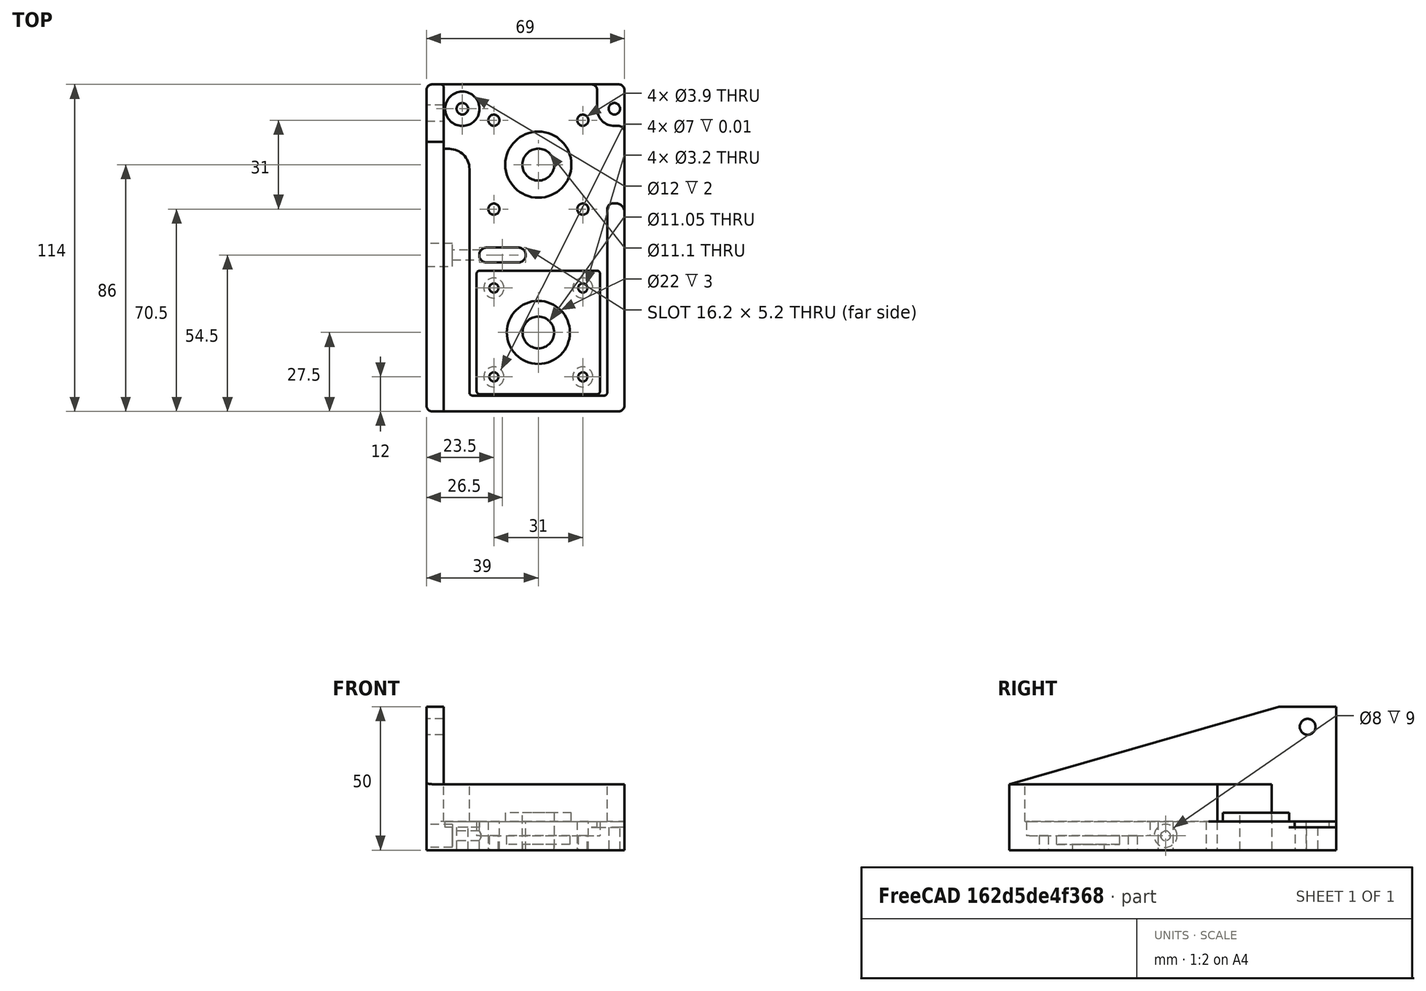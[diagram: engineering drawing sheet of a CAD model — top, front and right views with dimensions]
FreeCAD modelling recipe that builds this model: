
FCSTD DOCUMENT  (FreeCAD 0.19R)
Label: BeltDriveUnit3
License: All rights reserved
LicenseURL: http://en.wikipedia.org/wiki/All_rights_reserved
objects: Sketcher::SketchObject×14, PartDesign::Pocket×10, PartDesign::Fillet×10, PartDesign::Pad×4, PartDesign::Body×1, Mesh::Feature×1
note: 63 computed .brp shape members not serialized (recipe doc carries the construction recipe); baked Part::Feature solids carry a one-line shape summary decoded from their .brp

FEATURE [Sketcher::SketchObject] Sketch
  FullyConstrained = false
  MapMode = 5
  Support = -> [XY_Plane]
  sketch-geometry (17):
    g0: LineSegment StartX=-33 StartY=28 StartZ=0 EndX=30 EndY=28 EndZ=0
    g1: LineSegment StartX=30 StartY=28 StartZ=0 EndX=30 EndY=-86 EndZ=0
    g2: LineSegment StartX=30 StartY=-86 StartZ=0 EndX=-33 EndY=-86 EndZ=0
    g3: LineSegment StartX=-33 StartY=-86 StartZ=0 EndX=-33 EndY=28 EndZ=0
    g4: LineSegment StartX=-21 StartY=21 StartZ=0 EndX=21 EndY=21 EndZ=0
    g5: LineSegment StartX=21 StartY=21 StartZ=0 EndX=21 EndY=-21 EndZ=0
    g6: LineSegment StartX=21 StartY=-21 StartZ=0 EndX=-21 EndY=-21 EndZ=0
    g7: LineSegment StartX=-21 StartY=-21 StartZ=0 EndX=-21 EndY=21 EndZ=0
    g8: Circle CenterX=-15.5 CenterY=15.5 CenterZ=0 NormalX=0 NormalY=0 NormalZ=1 AngleXU=0 Radius=1.95
    g9: Circle CenterX=15.5 CenterY=15.5 CenterZ=0 NormalX=0 NormalY=0 NormalZ=1 AngleXU=0 Radius=1.95
    g10: Circle CenterX=-15.5 CenterY=-15.5 CenterZ=0 NormalX=0 NormalY=0 NormalZ=1 AngleXU=0 Radius=1.95
    g11: Circle CenterX=15.5 CenterY=-15.5 CenterZ=0 NormalX=0 NormalY=0 NormalZ=1 AngleXU=0 Radius=1.95
    g12: Circle CenterX=0 CenterY=-58.5 CenterZ=0 NormalX=0 NormalY=0 NormalZ=1 AngleXU=0 Radius=5.525
    g13: Circle CenterX=-15.5 CenterY=-43 CenterZ=0 NormalX=0 NormalY=0 NormalZ=1 AngleXU=0 Radius=1.6
    g14: Circle CenterX=15.5 CenterY=-43 CenterZ=0 NormalX=0 NormalY=0 NormalZ=1 AngleXU=0 Radius=1.6
    g15: Circle CenterX=-15.5 CenterY=-74 CenterZ=0 NormalX=0 NormalY=0 NormalZ=1 AngleXU=0 Radius=1.6
    g16: Circle CenterX=15.5 CenterY=-74 CenterZ=0 NormalX=0 NormalY=0 NormalZ=1 AngleXU=0 Radius=1.6
  constraints (44):
    c: Coincident(g0,g1)
    c: Coincident(g1,g2)
    c: Coincident(g2,g3)
    c: Coincident(g3,g0)
    c: Horizontal(g2)
    c: Vertical(g1)
    c: Vertical(g3)
    c: Coincident(g4,g5)
    c: Coincident(g5,g6)
    c: Coincident(g6,g7)
    c: Coincident(g7,g4)
    c: Horizontal(g4)
    c: Horizontal(g6)
    c: Vertical(g5)
    c: Vertical(g7)
    c: Equal(g5,g4)
    c: Distance(g5) = 42
    c: Symmetric(g4,g6,g-1)
    c: Distance(g4,g0) = 7
    c: Diameter(g11) = 3.9
    c: Equal(g11,g10)
    c: Equal(g11,g8)
    c: Equal(g11,g9)
    c: Distance(g9,g8) = 31
    c: Symmetric(g9,g8,g-2)
    c: Distance(g10,g8) = 31
    c: DistanceY(g11,g9) = 31
    c: DistanceX(g10,g11) = 31
    c: Symmetric(g9,g10,g-1)
    c: Diameter(g16) = 3.2
    c: Equal(g16,g14)
    c: Equal(g16,g13)
    c: Equal(g16,g15)
    c: Symmetric(g14,g13,g-2)
    c: Symmetric(g16,g15,g-2)
    c: Symmetric(g16,g13,g12)
    c: PointOnObject(g12,g-2)
    c: Distance(g14,g13) = 31
    c: Distance(g16,g14) = 31
    c: Distance(g-1,g12) = 58.5
    c: Diameter(g12) = 11.05
    c: DistanceY(g1) = -86
    c: DistanceX(g0) = 30
    c: DistanceX(g0) = -33
FEATURE [PartDesign::Pad] Pad
  Direction = (1,1,1)
  Length = 10
  Length2 = 100
  Profile = -> Sketch
  Type = 0
FEATURE [Sketcher::SketchObject] Sketch004  label="StepperPlugArtillery"
  FullyConstrained = true
  MapMode = 5
  Placement = pos=(0,0,10) rot=(0,0,1;0rad)
  Support = -> [Pad]
  sketch-geometry (1):
    g0: Circle CenterX=0 CenterY=0 CenterZ=0 NormalX=0 NormalY=0 NormalZ=1 AngleXU=0 Radius=11.525
  constraints (2):
    c: Coincident(g0,g-1)
    c: Diameter(g0) = 23.05
FEATURE [PartDesign::Pad] Pad001
  BaseFeature = -> Pad
  Direction = (1,1,1)
  Length = 3
  Length2 = 100
  Profile = -> Sketch004
  Type = 0
FEATURE [Sketcher::SketchObject] Sketch003  label="BearingBore"
  FullyConstrained = false
  MapMode = 5
  Placement = pos=(0,0,13) rot=(0,0,1;0rad)
  Support = -> [Pad001]
  sketch-geometry (1):
    g0: Circle CenterX=0 CenterY=0 CenterZ=0 NormalX=0 NormalY=0 NormalZ=1 AngleXU=0 Radius=5.55
  constraints (1):
    c: Diameter(g0) = 11.1
FEATURE [PartDesign::Pocket] Pocket
  BaseFeature = -> Pad001
  Length = 5
  Length2 = 100
  Profile = -> Sketch003
  Type = 1
FEATURE [Sketcher::SketchObject] Sketch006  label="StepperSocket"
  ExternalGeometry = -> [Pocket]
  FullyConstrained = true
  MapMode = 5
  Placement = pos=(0,0,10) rot=(0,0,1;0rad)
  Support = -> [Pocket]
  sketch-geometry (1):
    g0: Circle CenterX=0 CenterY=-58.5 CenterZ=0 NormalX=0 NormalY=0 NormalZ=1 AngleXU=0 Radius=11
  constraints (2):
    c: Coincident(g0,g-3)
    c: Diameter(g0) = 22
FEATURE [PartDesign::Pocket] Pocket001
  BaseFeature = -> Pocket
  Length = 8
  Length2 = 100
  Profile = -> Sketch006
  Type = 0
FEATURE [Sketcher::SketchObject] Sketch007
  ExternalGeometry = -> [Pocket001]
  FullyConstrained = true
  MapMode = 5
  Placement = pos=(0,0,0) rot=(1,0,0;3.14159rad)
  Support = -> [Pocket001]
  sketch-geometry (4):
    g0: Circle CenterX=-15.5 CenterY=74 CenterZ=0 NormalX=0 NormalY=0 NormalZ=1 AngleXU=0 Radius=3.5
    g1: Circle CenterX=15.5 CenterY=74 CenterZ=0 NormalX=0 NormalY=0 NormalZ=1 AngleXU=0 Radius=3.5
    g2: Circle CenterX=15.5 CenterY=43 CenterZ=0 NormalX=0 NormalY=0 NormalZ=1 AngleXU=0 Radius=3.5
    g3: Circle CenterX=-15.5 CenterY=43 CenterZ=0 NormalX=0 NormalY=0 NormalZ=1 AngleXU=0 Radius=3.5
  constraints (9):
    c: Diameter(g3) = 7
    c: Equal(g3,g1)
    c: Equal(g3,g2)
    c: Equal(g3,g0)
    c: Symmetric(g0,g2,g-3)
    c: Symmetric(g1,g3,g-3)
    c: Distance(g2,g1) = 31
    c: Distance(g3,g2) = 31
    c: Symmetric(g3,g2,g-2)
FEATURE [PartDesign::Pocket] Pocket002
  BaseFeature = -> Pocket001
  Length = 0.01
  Length2 = 100
  Profile = -> Sketch007
  Type = 0
FEATURE [Sketcher::SketchObject] Sketch008  label="Slot"
  ExternalGeometry = -> [Pocket002]
  FullyConstrained = true
  MapMode = 5
  Placement = pos=(0,0,10) rot=(0,0,1;0rad)
  Support = -> [Pocket002]
  sketch-geometry (11):
    g0: Circle CenterX=0 CenterY=0 CenterZ=0 NormalX=0 NormalY=0 NormalZ=1 AngleXU=0 Radius=18.5
    g1: Circle CenterX=0 CenterY=-58.5 CenterZ=0 NormalX=0 NormalY=0 NormalZ=1 AngleXU=0 Radius=6
    g2: LineSegment StartX=-18.0727 StartY=-3.95299 StartZ=0 EndX=-5.86143 EndY=-59.782 EndZ=0
    g3: ArcOfCircle CenterX=-18 CenterY=-31.5 CenterZ=0 NormalX=0 NormalY=0 NormalZ=1 AngleXU=0 Radius=2.6 StartAngle=1.5708 EndAngle=4.71239
    g4: ArcOfCircle CenterX=-7 CenterY=-31.5 CenterZ=0 NormalX=0 NormalY=0 NormalZ=1 AngleXU=0 Radius=2.6 StartAngle=4.71239 EndAngle=7.85398
    g5: LineSegment StartX=-18 StartY=-34.1 StartZ=0 EndX=-7 EndY=-34.1 EndZ=0
    g6: LineSegment StartX=-18 StartY=-28.9 StartZ=0 EndX=-7 EndY=-28.9 EndZ=0
    g7: Circle CenterX=-18 CenterY=-31.5 CenterZ=0 NormalX=0 NormalY=0 NormalZ=1 AngleXU=0 Radius=6
    g8: Circle CenterX=-7 CenterY=-31.5 CenterZ=0 NormalX=0 NormalY=0 NormalZ=1 AngleXU=0 Radius=6
    g9: LineSegment StartX=-15.5 StartY=-37.5 StartZ=0 EndX=-15.5 EndY=-79 EndZ=0
    g10: LineSegment StartX=-15.5 StartY=-31.5 StartZ=0 EndX=-15.5 EndY=-37.5 EndZ=0
  constraints (29):
    c: Diameter(g0) = 37
    c: Coincident(g0,g-1)
    c: Diameter(g1) = 12
    c: Coincident(g1,g-3)
    c: PointOnObject(g2,g0)
    c: PointOnObject(g2,g1)
    c: Tangent(g2,g0)
    c: Tangent(g1,g2)
    c: Tangent(g3,g6) = 1.5708
    c: Tangent(g3,g5) = -1.5708
    c: Tangent(g5,g4) = -1.5708
    c: Tangent(g6,g4) = 1.5708
    c: Horizontal(g5)
    c: Equal(g3,g4)
    c: Diameter(g7) = 12
    c: Coincident(g3,g7)
    c: Diameter(g8) = 12
    c: Coincident(g8,g4)
    c: Distance(g3,g3) = 5.2
    c: Distance(g6) = 11
    c: DistanceX(g4) = -7
    c: Vertical(g9)
    c: Distance(g9) = 41.5
    c: PointOnObject(g-5,g9)
    c: DistanceY(g-5,g9) = 5.5
    c: Vertical(g10)
    c: Distance(g10) = 6
    c: Coincident(g10,g9)
    c: DistanceY(g10,g3) = 0
FEATURE [PartDesign::Pocket] Pocket003
  BaseFeature = -> Pocket002
  Length = 5
  Length2 = 100
  Profile = -> Sketch008
  Type = 1
FEATURE [Sketcher::SketchObject] Sketch009  label="JackScrew"
  FullyConstrained = true
  MapMode = 5
  Placement = pos=(-33,0,0) rot=(0.57735,-0.57735,-0.57735;2.0944rad)
  Support = -> [Pocket003]
  sketch-geometry (1):
    g0: Circle CenterX=31.5 CenterY=5 CenterZ=0 NormalX=0 NormalY=0 NormalZ=1 AngleXU=0 Radius=1.7
  constraints (3):
    c: Diameter(g0) = 3.4
    c: DistanceY(g0) = 5
    c: DistanceX(g0) = 31.5
FEATURE [PartDesign::Pocket] Pocket004
  BaseFeature = -> Pocket003
  Length = 17
  Length2 = 100
  Profile = -> Sketch009
  Type = 0
FEATURE [Sketcher::SketchObject] Sketch014  label="Stiffernerring"
  ExternalGeometry = -> [Pocket004]
  FullyConstrained = true
  MapMode = 5
  Placement = pos=(0,0,10) rot=(0,0,1;0rad)
  Support = -> [Pocket004]
  sketch-geometry (8):
    g0: LineSegment StartX=-33 StartY=5.5 StartZ=0 EndX=-24 EndY=5.5 EndZ=0
    g1: LineSegment StartX=-24 StartY=5.5 StartZ=0 EndX=-24 EndY=-80.5 EndZ=0
    g2: LineSegment StartX=-24 StartY=-80.5 StartZ=0 EndX=24 EndY=-80.5 EndZ=0
    g3: LineSegment StartX=24 StartY=-80.5 StartZ=0 EndX=24 EndY=-13.5 EndZ=0
    g4: LineSegment StartX=24 StartY=-13.5 StartZ=0 EndX=30 EndY=-13.5 EndZ=0
    g5: LineSegment StartX=30 StartY=-13.5 StartZ=0 EndX=30 EndY=-86 EndZ=0
    g6: LineSegment StartX=30 StartY=-86 StartZ=0 EndX=-33 EndY=-86 EndZ=0
    g7: LineSegment StartX=-33 StartY=-86 StartZ=0 EndX=-33 EndY=5.5 EndZ=0
  constraints (22):
    c: Coincident(g0,g1)
    c: Vertical(g1)
    c: Coincident(g1,g2)
    c: Horizontal(g2)
    c: Coincident(g2,g3)
    c: Vertical(g3)
    c: Coincident(g3,g4)
    c: Coincident(g4,g5)
    c: Coincident(g5,g6)
    c: Coincident(g6,g7)
    c: Coincident(g7,g0)
    c: Horizontal(g0)
    c: Distance(g0) = 9
    c: Horizontal(g4)
    c: Distance(g4) = 6
    c: Distance(g2,g6) = 5.5
    c: PointOnObject(g4,g-5)
    c: DistanceY(g-6,g0) = 21
    c: Coincident(g5,g-5)
    c: Coincident(g6,g-4)
    c: Vertical(g7)
    c: DistanceY(g4) = -13.5
FEATURE [PartDesign::Pad] Pad002
  BaseFeature = -> Pocket004
  Direction = (1,1,1)
  Length = 13
  Length2 = 100
  Profile = -> Sketch014
  Type = 0
FEATURE [Sketcher::SketchObject] Sketch022  label="Gussett"
  ExternalGeometry = -> [Pad002]
  FullyConstrained = true
  MapMode = 5
  Placement = pos=(-33,0,0) rot=(0.57735,-0.57735,-0.57735;2.0944rad)
  Support = -> [Pad002]
  sketch-geometry (5):
    g0: LineSegment StartX=-28 StartY=0 StartZ=0 EndX=-28 EndY=50 EndZ=0
    g1: LineSegment StartX=-28 StartY=50 StartZ=0 EndX=-8 EndY=50 EndZ=0
    g2: LineSegment StartX=-8 StartY=50 StartZ=0 EndX=86 EndY=23 EndZ=0
    g3: LineSegment StartX=86 StartY=23 StartZ=0 EndX=86 EndY=0 EndZ=0
    g4: LineSegment StartX=86 StartY=0 StartZ=0 EndX=-28 EndY=0 EndZ=0
  constraints (13):
    c: Vertical(g0)
    c: Coincident(g0,g1)
    c: Horizontal(g1)
    c: Coincident(g1,g2)
    c: Coincident(g2,g3)
    c: Coincident(g4,g0)
    c: Horizontal(g4)
    c: DistanceX(g0) = -28
    c: DistanceY(g0) = 50
    c: DistanceX(g1,g1) = 20
    c: Coincident(g3,g-3)
    c: Coincident(g2,g-4)
    c: Coincident(g4,g3)
FEATURE [PartDesign::Pad] Pad003
  BaseFeature = -> Pad002
  Direction = (1,1,1)
  Length = 6
  Length2 = 100
  Profile = -> Sketch022
  Type = 0
FEATURE [Sketcher::SketchObject] Sketch023  label="GussetBolt"
  FullyConstrained = true
  MapMode = 5
  Placement = pos=(-39,0,0) rot=(0.57735,-0.57735,-0.57735;2.0944rad)
  Support = -> [Pad003]
  sketch-geometry (1):
    g0: Circle CenterX=-18 CenterY=43 CenterZ=0 NormalX=0 NormalY=0 NormalZ=1 AngleXU=0 Radius=2.75
  constraints (3):
    c: DistanceY(g0) = 43
    c: DistanceX(g0) = -18
    c: Diameter(g0) = 5.5
FEATURE [PartDesign::Pocket] Pocket005
  BaseFeature = -> Pad003
  Length = 9
  Length2 = 100
  Profile = -> Sketch023
  Type = 0
FEATURE [Sketcher::SketchObject] Sketch025  label="MountingBolteALlen"
  ExternalGeometry = -> [Pocket005]
  FullyConstrained = true
  MapMode = 5
  Placement = pos=(0,0,0) rot=(1,0,0;3.14159rad)
  Support = -> [Pocket005]
  sketch-geometry (2):
    g0: Circle CenterX=26.5 CenterY=-19.5 CenterZ=0 NormalX=0 NormalY=0 NormalZ=1 AngleXU=0 Radius=2
    g1: Circle CenterX=-26.5 CenterY=-19.5 CenterZ=0 NormalX=0 NormalY=0 NormalZ=1 AngleXU=0 Radius=2
  constraints (5):
    c: Diameter(g0) = 4
    c: DistanceX(g-3,g0) = 11
    c: DistanceY(g0,g-3) = 4
    c: Symmetric(g0,g1,g-2)
    c: Diameter(g1) = 4
FEATURE [PartDesign::Pocket] Pocket006
  BaseFeature = -> Pocket005
  Length = 16
  Length2 = 100
  Profile = -> Sketch025
  Type = 0
FEATURE [Sketcher::SketchObject] Sketch026  label="MountingBoltReleifs"
  ExternalGeometry = -> [Pocket006]
  FullyConstrained = true
  MapMode = 5
  Placement = pos=(0,0,10) rot=(0,0,1;0rad)
  Support = -> [Pocket006]
  sketch-geometry (5):
    g0: ArcOfCircle CenterX=26.5 CenterY=19.5 CenterZ=0 NormalX=0 NormalY=0 NormalZ=1 AngleXU=0 Radius=6 StartAngle=3.14159 EndAngle=4.71239
    g1: Circle CenterX=-26.5 CenterY=19.5 CenterZ=0 NormalX=0 NormalY=0 NormalZ=1 AngleXU=0 Radius=6
    g2: LineSegment StartX=26.5 StartY=13.5 StartZ=0 EndX=46.5 EndY=13.5 EndZ=0
    g3: LineSegment StartX=20.5 StartY=46.38 StartZ=0 EndX=20.5 EndY=19.5 EndZ=0
    g4: LineSegment StartX=20.5 StartY=46.38 StartZ=0 EndX=46.5 EndY=13.5 EndZ=0
  constraints (12):
    c: Coincident(g1,g-3)
    c: Diameter(g1) = 12
    c: Diameter(g0) = 12
    c: Tangent(g0,g2) = -1.5708
    c: Horizontal(g2)
    c: Tangent(g3,g0) = -1.5708
    c: Coincident(g0,g-4)
    c: Distance(g2) = 20
    c: Vertical(g3)
    c: Coincident(g4,g3)
    c: Coincident(g4,g2)
    c: Distance(g3) = 26.88
FEATURE [PartDesign::Pocket] Pocket007
  BaseFeature = -> Pocket006
  Length = 2
  Length2 = 100
  Profile = -> Sketch026
  Type = 0
FEATURE [Sketcher::SketchObject] Sketch027  label="JackScrewspace"
  FullyConstrained = true
  MapMode = 5
  Placement = pos=(-39,0,0) rot=(0.57735,-0.57735,-0.57735;2.0944rad)
  Support = -> [Pocket007]
  sketch-geometry (1):
    g0: Circle CenterX=31.5 CenterY=5 CenterZ=0 NormalX=0 NormalY=0 NormalZ=1 AngleXU=0 Radius=4
  constraints (3):
    c: DistanceX(g-1,g0) = 31.5
    c: DistanceY(g0) = 5
    c: Diameter(g0) = 8
FEATURE [PartDesign::Pocket] Pocket008
  BaseFeature = -> Pocket007
  Length = 9
  Length2 = 100
  Profile = -> Sketch027
  Type = 0
FEATURE [Sketcher::SketchObject] Sketch028  label="StepperSocket001"
  ExternalGeometry = -> [Pocket008]
  FullyConstrained = true
  MapMode = 5
  Placement = pos=(0,0,10) rot=(0,0,1;0rad)
  Support = -> [Pocket008]
  sketch-geometry (4):
    g0: LineSegment StartX=-21.5 StartY=-37 StartZ=0 EndX=21.5 EndY=-37 EndZ=0
    g1: LineSegment StartX=21.5 StartY=-37 StartZ=0 EndX=21.5 EndY=-80 EndZ=0
    g2: LineSegment StartX=21.5 StartY=-80 StartZ=0 EndX=-21.5 EndY=-80 EndZ=0
    g3: LineSegment StartX=-21.5 StartY=-80 StartZ=0 EndX=-21.5 EndY=-37 EndZ=0
  constraints (11):
    c: Coincident(g0,g1)
    c: Coincident(g1,g2)
    c: Coincident(g2,g3)
    c: Coincident(g3,g0)
    c: Horizontal(g2)
    c: Vertical(g1)
    c: Vertical(g3)
    c: Symmetric(g1,g0,g-3)
    c: Equal(g0,g3)
    c: Distance(g0) = 43
    c: Perpendicular(g0,g3)
FEATURE [PartDesign::Pocket] Pocket009
  BaseFeature = -> Pocket008
  Length = 5
  Length2 = 100
  Profile = -> Sketch028
  Type = 0
FEATURE [PartDesign::Fillet] Fillet
  Base = -> Pocket009 [Edge62,Edge123,Edge92]
  BaseFeature = -> Pocket009
  Radius = 2
  SupportTransform = false
FEATURE [PartDesign::Fillet] Fillet001
  Base = -> Fillet [Edge131]
  BaseFeature = -> Fillet
  Radius = 7
  SupportTransform = false
FEATURE [PartDesign::Fillet] Fillet002
  Base = -> Fillet001 [Edge52]
  BaseFeature = -> Fillet001
  Radius = 3
  SupportTransform = false
FEATURE [PartDesign::Fillet] Fillet003
  Base = -> Fillet002 [Edge29]
  BaseFeature = -> Fillet002
  Radius = 2
  SupportTransform = false
FEATURE [PartDesign::Fillet] Fillet004
  Base = -> Fillet003 [Edge40]
  BaseFeature = -> Fillet003
  Radius = 2
  SupportTransform = false
FEATURE [PartDesign::Fillet] Fillet005
  Base = -> Fillet004 [Edge71,Edge6]
  BaseFeature = -> Fillet004
  Radius = 2
  SupportTransform = false
FEATURE [PartDesign::Fillet] Fillet006
  Base = -> Fillet005 [Edge89]
  BaseFeature = -> Fillet005
  Radius = 1
  SupportTransform = false
FEATURE [PartDesign::Fillet] Fillet007
  Base = -> Fillet006 [Edge35]
  BaseFeature = -> Fillet006
  Radius = 1
  SupportTransform = false
FEATURE [PartDesign::Fillet] Fillet008
  Base = -> Fillet007 [Edge85,Edge87,Edge84,Edge82]
  BaseFeature = -> Fillet007
  Radius = 1
  SupportTransform = false
FEATURE [PartDesign::Fillet] Fillet009
  Base = -> Fillet008 [Edge75]
  BaseFeature = -> Fillet008
  Radius = 1
  SupportTransform = false
FEATURE [PartDesign::Body] Body
  Group = -> [Sketch,Pad,Sketch003,Sketch004,Pad001,Pocket,Sketch006,Pocket001,Sketch007,Pocket002,Sketch008,Pocket003,Sketch009,Pocket004,Sketch014,Pad002,Sketch022,Pad003,Sketch023,Pocket005,Sketch025,Pocket006,Sketch026,Pocket007,Sketch027,Pocket008,Sketch028,Pocket009,Fillet,Fillet001,Fillet002,Fillet003,Fillet004,Fillet005,Fillet006,Fillet007,Fillet008,Fillet009]
  Origin = -> Origin
  Tip = -> Fillet009
FEATURE [Mesh::Feature] Mesh  label="Fillet009 (Meshed)"
